# Revit family: 306_62bc3c21313b430dad3193208a2377
name_source: partatom
category: Pipe Accessories
units: mm (PartAtom-declared; Revit-internal decimal feet)

## family parameters
Always vertical = Yes
Cut with Voids When Loaded = No
Part Type = Valve - Breaks Into
Round Connector Dimension = Use Diameter
Shared = No
Work Plane-Based = No

## types (14) — shared parameters
CAT0 = Yes
Description = 3-way rotary mixing valve VRG131, PN10 internal thread
L2D_Min = 3048 mm
MC = No
Manufacturer = ESBE
QmdConnectorList = 301;D;302;D
URL = http://www.esbe.eu
magiPartTypeId = 306
magiProductFamilyId = 62bc3c21313b430dad3193208a2377

## per-type parameters (varying)
| type | A | C | CenSd_NR_6 | D | D11 | L2D | LM | NR | W2D | X1 | X2 | X2__ve | Y0 | Y3 | Y6 | Y7 | Y9 | Z5 | Z5__ve | ZA1 | magiProductId |
| VRG131 15-0.4 RP 1/2 | 36 mm  [stored 0.11811 ft] | 32 mm  [stored 0.104987 ft] | 8 mm  [stored 0.0262467 ft] | 15 mm | 16 mm  [stored 0.0524934 ft] | 72 mm | 56 mm | 10 mm  [stored 0.0328084 ft] | 15 mm  [stored 0.0492126 ft] | 36 mm  [stored 0.11811 ft] | 8 mm  [stored 0.0262467 ft] | -8 mm | 8 mm  [stored 0.0262467 ft] | 20 mm  [stored 0.0656168 ft] | 19 mm | 17 mm | 16 mm  [stored 0.0524934 ft] | 8 mm  [stored 0.0262467 ft] | -8 mm | 28 mm | 58d4c82f30bd4e55b3f474f5813e1a |
| VRG131 50-40 RP 2 | 60 mm | 46 mm  [stored 0.150919 ft] | 28 mm | 50 mm | 16 mm  [stored 0.0524934 ft] | 120 mm | 94 mm | 33 mm | 50 mm  [stored 0.164042 ft] | 60 mm | 13 mm  [stored 0.0426509 ft] | -13 mm | 25 mm  [stored 0.082021 ft] | 34 mm  [stored 0.111549 ft] | 33 mm | 31 mm | 30 mm  [stored 0.0984252 ft] | 13 mm  [stored 0.0426509 ft] | -13 mm | 47 mm  [stored 0.154199 ft] | 2631535a68e346f9b0337476bcddd0 |
| VRG131 40-25 RP 1½ | 53 mm  [stored 0.173885 ft] | 44 mm  [stored 0.144357 ft] | 23 mm | 40 mm | 14 mm  [stored 0.0459318 ft] | 106 mm | 83 mm | 26 mm  [stored 0.0853018 ft] | 40 mm  [stored 0.131234 ft] | 53 mm  [stored 0.173885 ft] | 12 mm  [stored 0.0393701 ft] | -12 mm | 20 mm  [stored 0.0656168 ft] | 30 mm  [stored 0.0984252 ft] | 29 mm | 27 mm | 26 mm  [stored 0.0853018 ft] | 12 mm  [stored 0.0393701 ft] | -12 mm | 41 mm  [stored 0.134514 ft] | fde771f88d4248d295f412caacc72a |
| VRG131 32-16 RP 1 1/4 | 47 mm  [stored 0.154199 ft] | 37 mm  [stored 0.121391 ft] | 18 mm  [stored 0.0590551 ft] | 32 mm | 16 mm  [stored 0.0524934 ft] | 94 mm | 73 mm | 21 mm | 32 mm  [stored 0.104987 ft] | 47 mm  [stored 0.154199 ft] | 10 mm  [stored 0.0328084 ft] | -10 mm  [stored -0.0328084 ft] | 16 mm  [stored 0.0524934 ft] | 26 mm  [stored 0.0853018 ft] | 25 mm  [stored 0.082021 ft] | 23 mm | 22 mm | 10 mm  [stored 0.0328084 ft] | -10 mm  [stored -0.0328084 ft] | 37 mm  [stored 0.121391 ft] | d1da27c8818941bfaf8d691d4647e4 |
| VRG131 25-6.3 RP 1 | 41 mm  [stored 0.134514 ft] | 34 mm  [stored 0.111549 ft] | 14 mm  [stored 0.0459318 ft] | 25 mm | 16 mm  [stored 0.0524934 ft] | 82 mm | 64 mm | 16 mm  [stored 0.0524934 ft] | 25 mm  [stored 0.082021 ft] | 41 mm  [stored 0.134514 ft] | 9 mm  [stored 0.0295276 ft] | -9 mm | 13 mm  [stored 0.0426509 ft] | 22 mm | 21 mm | 20 mm  [stored 0.0656168 ft] | 19 mm | 9 mm  [stored 0.0295276 ft] | -9 mm | 32 mm  [stored 0.104987 ft] | 2211f80e7537472e8b2a45ba9aca96 |
| VRG131 25-10 RP 1 | 41 mm  [stored 0.134514 ft] | 34 mm  [stored 0.111549 ft] | 14 mm  [stored 0.0459318 ft] | 25 mm | 16 mm  [stored 0.0524934 ft] | 82 mm | 64 mm | 16 mm  [stored 0.0524934 ft] | 25 mm  [stored 0.082021 ft] | 41 mm  [stored 0.134514 ft] | 9 mm  [stored 0.0295276 ft] | -9 mm | 13 mm  [stored 0.0426509 ft] | 22 mm | 21 mm | 20 mm  [stored 0.0656168 ft] | 19 mm | 9 mm  [stored 0.0295276 ft] | -9 mm | 32 mm  [stored 0.104987 ft] | f4ee4c51eb6d4cb08a85d4f206afd4 |
| VRG131 20-6.3 RP 3/4 | 36 mm  [stored 0.11811 ft] | 32 mm  [stored 0.104987 ft] | 11 mm | 20 mm | 16 mm  [stored 0.0524934 ft] | 72 mm | 56 mm | 13 mm  [stored 0.0426509 ft] | 20 mm  [stored 0.0656168 ft] | 36 mm  [stored 0.11811 ft] | 8 mm  [stored 0.0262467 ft] | -8 mm | 10 mm  [stored 0.0328084 ft] | 20 mm  [stored 0.0656168 ft] | 19 mm | 17 mm | 16 mm  [stored 0.0524934 ft] | 8 mm  [stored 0.0262467 ft] | -8 mm | 28 mm | 080b64bc50424b9390c66885d0c555 |
| VRG131 20-4 RP 3/4 | 36 mm  [stored 0.11811 ft] | 32 mm  [stored 0.104987 ft] | 11 mm | 20 mm | 16 mm  [stored 0.0524934 ft] | 72 mm | 56 mm | 13 mm  [stored 0.0426509 ft] | 20 mm  [stored 0.0656168 ft] | 36 mm  [stored 0.11811 ft] | 8 mm  [stored 0.0262467 ft] | -8 mm | 10 mm  [stored 0.0328084 ft] | 20 mm  [stored 0.0656168 ft] | 19 mm | 17 mm | 16 mm  [stored 0.0524934 ft] | 8 mm  [stored 0.0262467 ft] | -8 mm | 28 mm | 0acf1327115d437b8f42ab43a5e241 |
| VRG131 20-2.5 RP 3/4 | 36 mm  [stored 0.11811 ft] | 32 mm  [stored 0.104987 ft] | 11 mm | 20 mm | 16 mm  [stored 0.0524934 ft] | 72 mm | 56 mm | 13 mm  [stored 0.0426509 ft] | 20 mm  [stored 0.0656168 ft] | 36 mm  [stored 0.11811 ft] | 8 mm  [stored 0.0262467 ft] | -8 mm | 10 mm  [stored 0.0328084 ft] | 20 mm  [stored 0.0656168 ft] | 19 mm | 17 mm | 16 mm  [stored 0.0524934 ft] | 8 mm  [stored 0.0262467 ft] | -8 mm | 28 mm | 81a1d8d97ef64c06ae8cb049536fb0 |
| VRG131 15-4 RP 1/2 | 36 mm  [stored 0.11811 ft] | 32 mm  [stored 0.104987 ft] | 8 mm  [stored 0.0262467 ft] | 15 mm | 16 mm  [stored 0.0524934 ft] | 72 mm | 56 mm | 10 mm  [stored 0.0328084 ft] | 15 mm  [stored 0.0492126 ft] | 36 mm  [stored 0.11811 ft] | 8 mm  [stored 0.0262467 ft] | -8 mm | 8 mm  [stored 0.0262467 ft] | 20 mm  [stored 0.0656168 ft] | 19 mm | 17 mm | 16 mm  [stored 0.0524934 ft] | 8 mm  [stored 0.0262467 ft] | -8 mm | 28 mm | f979faadd4ff46d1bd7f9f94c31961 |
| VRG131 15-2.5 RP 1/2 | 36 mm  [stored 0.11811 ft] | 32 mm  [stored 0.104987 ft] | 8 mm  [stored 0.0262467 ft] | 15 mm | 16 mm  [stored 0.0524934 ft] | 72 mm | 56 mm | 10 mm  [stored 0.0328084 ft] | 15 mm  [stored 0.0492126 ft] | 36 mm  [stored 0.11811 ft] | 8 mm  [stored 0.0262467 ft] | -8 mm | 8 mm  [stored 0.0262467 ft] | 20 mm  [stored 0.0656168 ft] | 19 mm | 17 mm | 16 mm  [stored 0.0524934 ft] | 8 mm  [stored 0.0262467 ft] | -8 mm | 28 mm | 0d17fbdf6f8f4230809b1147ba1e11 |
| VRG131 15-1.6 RP 1/2 | 36 mm  [stored 0.11811 ft] | 32 mm  [stored 0.104987 ft] | 8 mm  [stored 0.0262467 ft] | 15 mm | 16 mm  [stored 0.0524934 ft] | 72 mm | 56 mm | 10 mm  [stored 0.0328084 ft] | 15 mm  [stored 0.0492126 ft] | 36 mm  [stored 0.11811 ft] | 8 mm  [stored 0.0262467 ft] | -8 mm | 8 mm  [stored 0.0262467 ft] | 20 mm  [stored 0.0656168 ft] | 19 mm | 17 mm | 16 mm  [stored 0.0524934 ft] | 8 mm  [stored 0.0262467 ft] | -8 mm | 28 mm | aec2caf0b1934e73bf522326075cd7 |
| VRG131 15-1.0 RP 1/2 | 36 mm  [stored 0.11811 ft] | 32 mm  [stored 0.104987 ft] | 8 mm  [stored 0.0262467 ft] | 15 mm | 16 mm  [stored 0.0524934 ft] | 72 mm | 56 mm | 10 mm  [stored 0.0328084 ft] | 15 mm  [stored 0.0492126 ft] | 36 mm  [stored 0.11811 ft] | 8 mm  [stored 0.0262467 ft] | -8 mm | 8 mm  [stored 0.0262467 ft] | 20 mm  [stored 0.0656168 ft] | 19 mm | 17 mm | 16 mm  [stored 0.0524934 ft] | 8 mm  [stored 0.0262467 ft] | -8 mm | 28 mm | b14d8f5853d4499f9e45ec8ff9d9a0 |
| VRG131 15-0.63 RP 1/2 | 36 mm  [stored 0.11811 ft] | 32 mm  [stored 0.104987 ft] | 8 mm  [stored 0.0262467 ft] | 15 mm | 16 mm  [stored 0.0524934 ft] | 72 mm | 56 mm | 10 mm  [stored 0.0328084 ft] | 15 mm  [stored 0.0492126 ft] | 36 mm  [stored 0.11811 ft] | 8 mm  [stored 0.0262467 ft] | -8 mm | 8 mm  [stored 0.0262467 ft] | 20 mm  [stored 0.0656168 ft] | 19 mm | 17 mm | 16 mm  [stored 0.0524934 ft] | 8 mm  [stored 0.0262467 ft] | -8 mm | 28 mm | f07aa8e2a1a44b789df94a2c0eebd2 |

note: column(s) folded — value = type name in every type: magiProductCode

note: [stored X ft] marks values corroborated as IEEE doubles in the binary element streams (Revit-internal decimal feet)

## geometry (parser evidence)
native form markers: Sweep x1
no freeform markers — native parametric forms only
